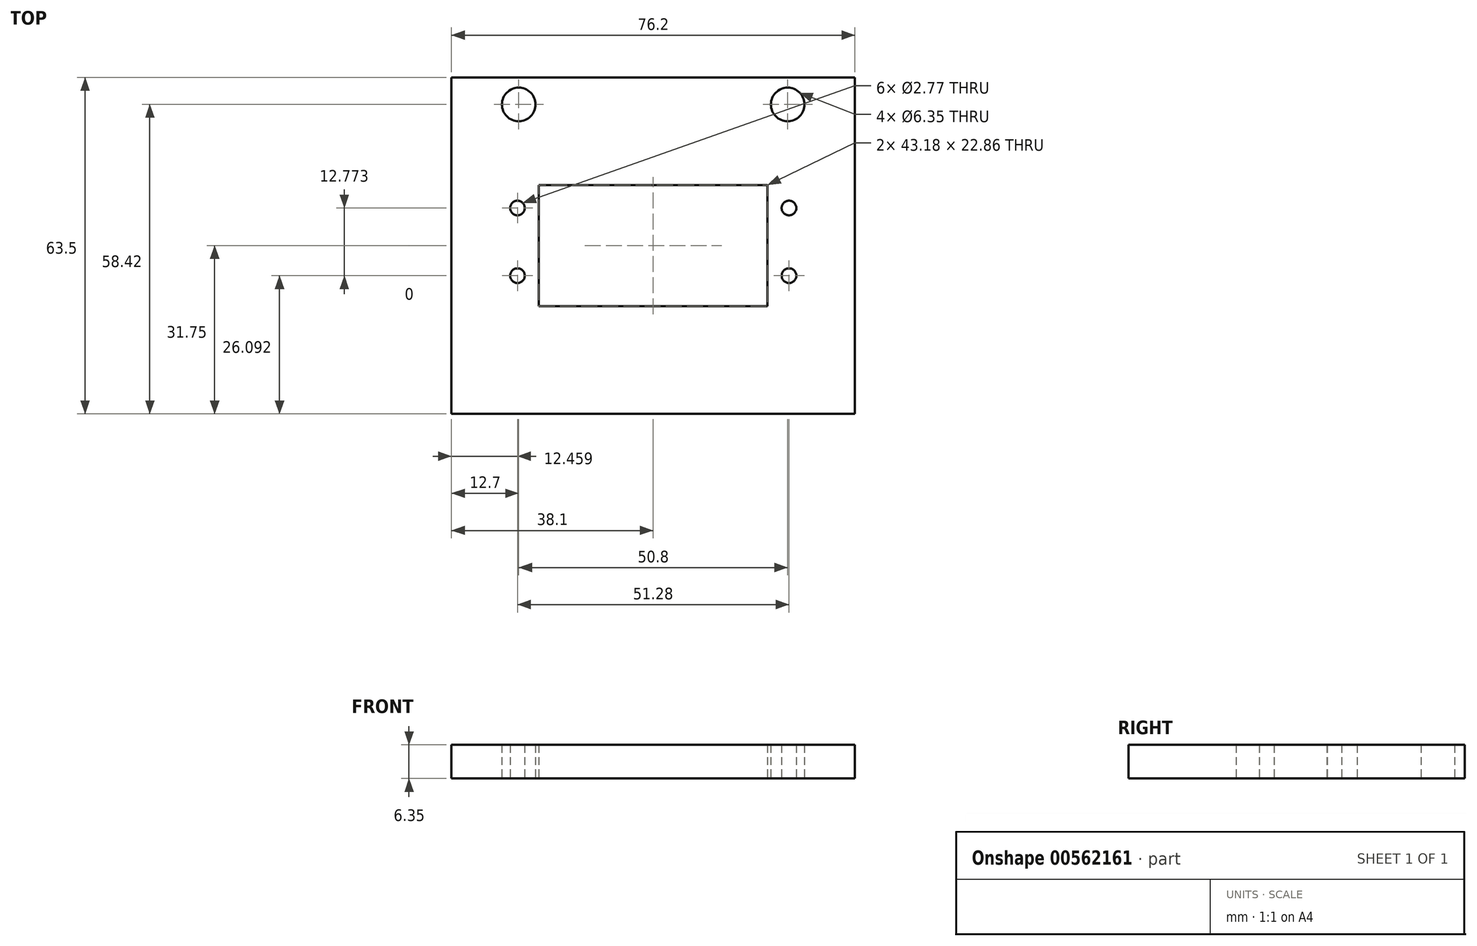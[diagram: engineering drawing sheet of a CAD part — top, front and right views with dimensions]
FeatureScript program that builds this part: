
annotation { "Feature Type Name" : "Feature", "Feature Type Description" : "" }
export const myFeature = defineFeature(function(context is Context, id is Id, definition is map)
    precondition{}
    {
        {
            var Q0;
            Q0=qCreatedBy(makeId("Top.planeOp"),FACE);
            var sketch = newSketch(context, id + "F0", { "sketchPlane" : qUnion([Q0])});
            skLineSegment(sketch, "E0.bottom", {"start": v(0, 0) * mm, "end": v(43.17, 0) * mm});
            skLineSegment(sketch, "E0.top", {"start": v(0, -22.86) * mm, "end": v(43.18, -22.86) * mm});
            skLineSegment(sketch, "E0.left", {"start": v(0, 0) * mm, "end": v(0, -22.86) * mm});
            skLineSegment(sketch, "E0.right", {"start": v(43.17, 0) * mm, "end": v(43.18, -22.86) * mm});
            skLineSegment(sketch, "E1.bottom", {"start": v(59.7, -43.18) * mm, "end": v(-16.51, -43.18) * mm});
            skLineSegment(sketch, "E1.top", {"start": v(59.69, 20.32) * mm, "end": v(-16.51, 20.32) * mm});
            skLineSegment(sketch, "E1.left", {"start": v(59.7, -43.18) * mm, "end": v(59.69, 20.32) * mm});
            skLineSegment(sketch, "E1.right", {"start": v(-16.5, -43.18) * mm, "end": v(-16.51, 20.32) * mm});
            skLineSegment(sketch, "E2", {"start": v(0, 0) * mm, "end": v(43.18, -22.86) * mm, "construction": true});
            skLineSegment(sketch, "E3", {"start": v(43.17, 0) * mm, "end": v(0, -22.86) * mm, "construction": true});
            skLineSegment(sketch, "E4", {"start": v(-16.51, 20.32) * mm, "end": v(59.7, -43.18) * mm, "construction": true});
            skLineSegment(sketch, "E5", {"start": v(59.7, 20.32) * mm, "end": v(-16.51, -43.18) * mm, "construction": true});
            skPoint(sketch, "E6", {"position": v(21.59, -11.43) * mm});
            skPoint(sketch, "E7", {"position": v(21.6, -11.43) * mm});
            skCircle(sketch, "E8", {"center": v(-3.81, 15.24) * mm, "radius": 3.18 * mm});
            skCircle(sketch, "E9", {"center": v(46.99, 15.24) * mm, "radius": 3.18 * mm});
            skCircle(sketch, "E10", {"center": v(-4.05, -4.31) * mm, "radius": 1.38 * mm});
            skCircle(sketch, "E11", {"center": v(-4.05, -17.09) * mm, "radius": 1.38 * mm});
            skCircle(sketch, "E12", {"center": v(47.23, -4.31) * mm, "radius": 1.39 * mm});
            skCircle(sketch, "E13", {"center": v(47.23, -17.09) * mm, "radius": 1.38 * mm});
            skSolve(sketch);
        }
        {
            var Q0;
            Q0=makeQuery(id+"F0.imprint","IMPRINT",FACE,{"disambiguationData":[TD([[makeQuery(id+"F0.imprint","IMPRINT",EDGE,{"derivedFrom":sQuery(id+"F0.wireOp",EDGE,"E0.bottom")}),1.0]])]});
            extrude(context, id + "F1", {"entities" : qUnion([Q0]), "depth" : 6.35 * mm, "offsetDistance" : 25.4 * mm});
        }
    });
